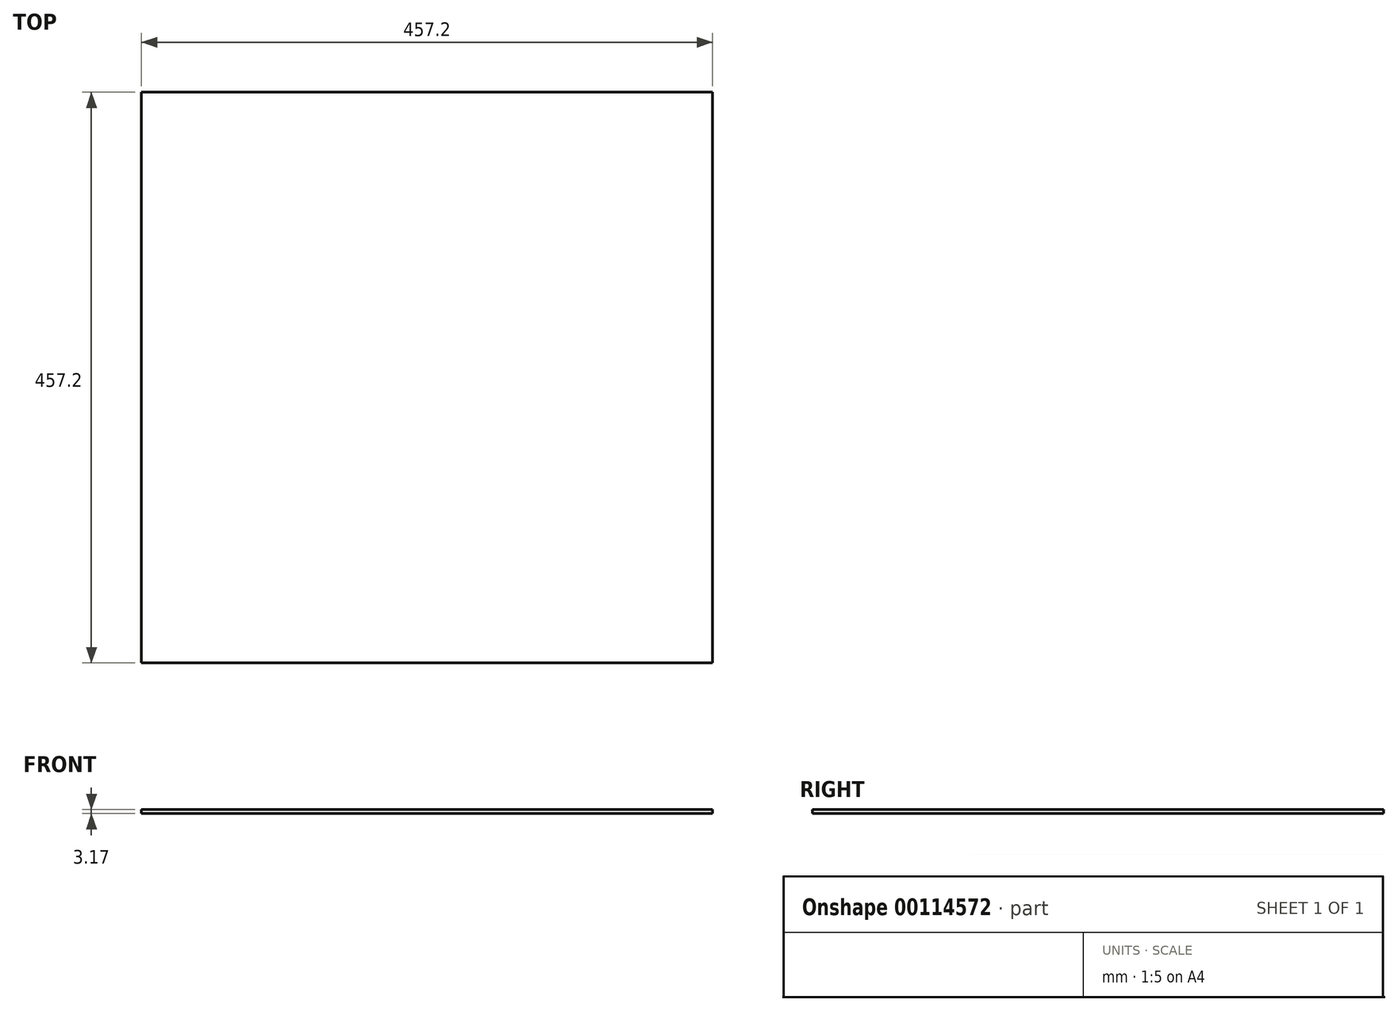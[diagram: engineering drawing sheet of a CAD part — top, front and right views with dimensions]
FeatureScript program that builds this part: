
annotation { "Feature Type Name" : "Feature", "Feature Type Description" : "" }
export const myFeature = defineFeature(function(context is Context, id is Id, definition is map)
    precondition{}
    {
        {
            var Q0;
            Q0=qCreatedBy(makeId("Top.planeOp"),FACE);
            var sketch = newSketch(context, id + "F0", { "sketchPlane" : qUnion([Q0])});
            skLineSegment(sketch, "E0.bottom", {"start": v(228.6, 228.6) * mm, "end": v(-228.6, 228.6) * mm});
            skLineSegment(sketch, "E0.top", {"start": v(228.6, -228.6) * mm, "end": v(-228.6, -228.6) * mm});
            skLineSegment(sketch, "E0.left", {"start": v(228.6, 228.6) * mm, "end": v(228.6, -228.6) * mm});
            skLineSegment(sketch, "E0.right", {"start": v(-228.6, 228.6) * mm, "end": v(-228.6, -228.6) * mm});
            skPoint(sketch, "E0.middle", {"position": v(0, 0) * mm});
            skSolve(sketch);
        }
        {
            var Q0;
            Q0 = qSketchRegion(id + "F0", true);
            extrude(context, id + "F1", {"entities" : qUnion([Q0]), "depth" : 3.17 * mm});
        }
    });
